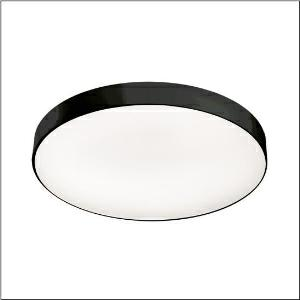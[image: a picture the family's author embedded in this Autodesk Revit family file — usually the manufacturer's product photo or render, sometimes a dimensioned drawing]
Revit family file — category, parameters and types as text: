
# Revit family: round_21_l_51mr38nd0421b
name_source: partatom
category: Lighting Fixtures
units: mm (PartAtom-declared; Revit-internal decimal feet)

## family parameters
Cut with Voids When Loaded = No
Host = Face
Light Source = No
Part Type = Normal
Room Calculation Point = No
Round Connector Dimension = Use Diameter
Shared = No

## types (1)
- Round 21 L (1 x LED, 12230 lm, 88.2 W, 4000K)
    Apparent Load = 88 VA
    CIE Flux Codes = 66 90 98 71 100
    Color Rendering = 80
    Color Temperature = 4000K
    Default Elevation = 1800 mm
    Description = Round 21 L, wall and ceiling luminaire, primary optical cover: micro prismatic cover, of PMMA, transparent, CAT 2 (L<= 3000cd/m²), light emission: direct/indirect distribution, primary light characteristic: symmetric, installation type: suspended mounting, surface-mounted, LED, rated luminous flux: 12.230lm, luminous efficacy: 139lm/W, light colour: 840, colour temperature: 4000K, with terminal, 5-pole, mains connection: 230V, AC, 50/60Hz, rated input power: 88W, housing, of aluminium, coated, black, diameter: 850mm, height: 62mm, protection rating (complete): IP40, insulation class (complete): insulation class I (protective earthing), certification: CE, impact resistance: IK04, permissible operating ambient temperature: -10..+35°C, packaging unit: 1 piece
    Height = 87 mm
    Lamp = 1 x LED
    Lamp Light Flux = 12230 lm
    Lamp Power = 88.2 W
    Lamp count = 1
    Length = 850 mm
    Luminous efficacy = 139 lm/W
    Manufacturer = Siteco
    ModVariant = No
    Model = 51MR38ND0421B
    Mounting Place = Ceiling
    Mounting Type = Surface mounted
    Number of Poles = 1
    OnlyDefault = Yes
    Power Factor = 1
    Product Name = Round 21 L
    Product group = wall and ceiling luminaire
    ProductGroupID = 303
    Protection Class = Protection class I
    Protection Degree = IP 40
    RLX_Detail_Level = 1
    RLX_Emergency_Light_Flux = 0 lm
    RLX_Emergency_Type = 0
    RLX_Emergency_Type_DB = No
    RlxData = <blob elided: 28709 chars, md5=05b7c3ea>
    Socket = socket
    Standby Power = 0 W
    System Light Flux = 12230 lm
    System Power = 88 W
    Type Comments = Product without accessories
    Type Image = l_1258326.jpg
    URL = http://relux.com
    VarID = ---
    Voltage = 0 V
    Weight = 0.00 kg
    Width = 0 mm  [stored 0 ft]

note: [stored X ft] marks values corroborated as IEEE doubles in the binary element streams (Revit-internal decimal feet)

## geometry (parser evidence)
native form markers: Blend x4, Sweep x12
no freeform markers — native parametric forms only
